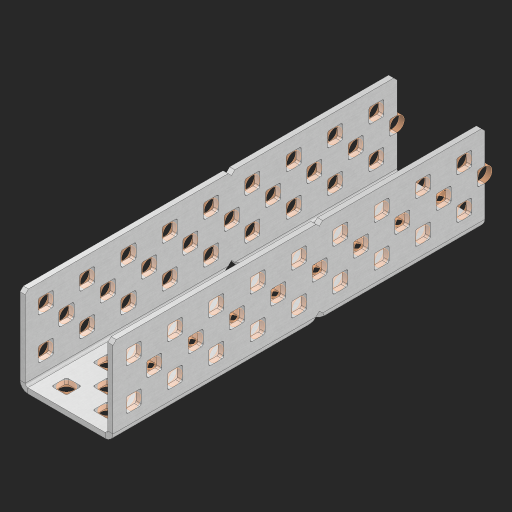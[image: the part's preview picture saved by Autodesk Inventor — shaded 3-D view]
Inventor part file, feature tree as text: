
AUTODESK INVENTOR PART (.ipt)
format: ipt  version: 2023 (Build 270158000, 158)  size: 1,304,064 bytes
history: native  units: in
note: dims shown in document units (in); Inventor stores cm internally (conversion verified against a paired STEP export)
features: other x114, extrude x106, sheet_metal_op x8, sketch x7, mirror x3, pattern_linear x2, chamfer x1
ambient origin geometry x8: Origin, YZ Plane, XZ Plane, XY Plane, X Axis, Y Axis, Z Axis, Center Point
bodies: Solid1 (feature_tree), Body (feature_tree)
feature tree (241):
  sheet_metal_op  "Flanges"
  sheet_metal_op  "Body Pattern"
  pattern_linear  "Center Pattern"  Spacing1=1.0in  [1 undecoded]
  other  "Arc Length"
  mirror  "Notch Mirror"
  pattern_linear  "Notch Pattern"  Spacing1=0.25in  [1 undecoded]
  other  "Diagonal Plane"
  mirror  "Flange 1"
  mirror  "Flange 2"
  chamfer  "End Chamfer"
  sketch  "Sketch1"  dims[d0=1.0in]
  other  "Plate1"
  sketch  "Sketch2"  dims[d1=4.5in]
  other  "Plate2"
  sheet_metal_op  "Bend1"
  sheet_metal_op  "Corner1"
  sketch  "Sketch8"  dims[d2=0.0625in]
  sketch  "Sketch9"  dims[d3=0.0625in]
  other  "Srf91"
  sheet_metal_op  "Body Pattern Sketch"
  other  "Srf92"
  sketch  "Sketch13"  dims[d4=0.0312in]
  sketch  "Sketch15"  dims[d5=0.125in]
  sketch  "Sketch16"  dims[d6=0.0625in d7=1.0in d8=90.0deg d9=0.0312in d10=0.25in d11=0.0625in d12=0.0625in d49=0.182in d50=0.02in d52=0.25in d53=0.0625in d54=0.0in d55=0.172in d56=1.0in d57=0.0in d60=3.5433in d62=0.5in d63=0.7874in d65=0.5in d85=0.1473in d86=0.1782in d88=0.04in d89=0.0625in d90=0.0in d91=0.04in d92=0.0491in d95=2.5in d96=0.04in d97=0.25in d98=45.0deg d99=0.25in d102=2.497in d106=0.182in d107=0.02in d108=0.5in d110=0.0625in d111=0.0in d112=0.172in d113=0.5in d114=0.0in d117=0.5in d118=0.5in d131=0.25in d132=0.25in]
  other  "Srf786"
  other  "Srf889"
  other  "Srf890"
  other  "Srf891"
  other  "Srf892"
  other  "Srf893"
  other  "Srf894"
  other  "Srf895"
  other  "Srf896"
  other  "Srf1315"
  other  "Srf1316"
  other  "Srf1317"
  other  "Srf1325"
  other  "Srf1326"
  other  "Srf1327"
  other  "Srf1328"
  other  "Srf1329"
  other  "Srf1330"
  other  "Srf1331"
  other  "Srf1332"
  other  "Srf1374"
  other  "Srf1375"
  other  "Srf1376"
  other  "Srf1384"
  other  "Srf1385"
  other  "Srf1386"
  other  "Srf1387"
  other  "Srf1388"
  other  "Srf1389"
  other  "Srf1390"
  other  "Srf1391"
  other  "Srf1433"
  other  "Srf1434"
  other  "Srf1473"
  other  "Srf1474"
  other  "Srf1475"
  other  "Srf1476"
  other  "Srf1477"
  other  "Srf1478"
  other  "Srf1479"
  other  "Srf1480"
  other  "Srf1481"
  other  "Srf1500"
  other  "Srf1501"
  other  "Srf1502"
  other  "Srf1503"
  other  "Srf1504"
  other  "Srf1505"
  other  "Srf1506"
  other  "Srf1507"
  other  "Srf1508"
  other  "Srf1509"
  other  "Srf1510"
  other  "Srf1511"
  other  "Srf1512"
  other  "Srf1513"
  other  "Srf1514"
  other  "Srf1515"
  other  "Srf1538"
  other  "Srf1539"
  other  "Srf1540"
  other  "Srf1541"
  other  "Srf1542"
  other  "Srf1543"
  other  "Srf1544"
  other  "Srf1545"
  other  "Srf1546"
  other  "Srf1547"
  other  "Srf1548"
  other  "Srf1549"
  other  "Srf1550"
  other  "Srf1551"
  other  "Srf1552"
  other  "Srf1553"
  other  "Srf1576"
  other  "Srf1577"
  other  "Srf1578"
  other  "Srf1579"
  other  "Srf1580"
  other  "Srf1581"
  other  "Srf1582"
  other  "Srf1583"
  other  "Srf1584"
  other  "Srf1585"
  other  "Srf1586"
  other  "Srf1587"
  other  "Srf1588"
  other  "Srf1589"
  other  "Srf1590"
  other  "Srf1591"
  other  "Srf1614"
  other  "Srf1615"
  other  "Srf1616"
  other  "Srf1617"
  other  "Srf1618"
  other  "Srf1619"
  other  "Srf1620"
  other  "Srf1621"
  other  "Srf1622"
  other  "Srf1623"
  other  "Srf1624"
  other  "Srf1625"
  other  "Srf1626"
  other  "Srf1627"
  other  "Srf1628"
  other  "Srf1629"
  sheet_metal_op  "Body Stamp"
  sheet_metal_op  "Body Circle"
  other  "Center Stamp"
  other  "Center Circle"
  sheet_metal_op  "Notch"
  extrude  "ExtrusionSrf92"  Depth=0.0625in
  extrude  "ExtrusionSrf889"  Depth=0.0625in
  extrude  "ExtrusionSrf890"  Depth=0.182in
  extrude  "ExtrusionSrf891"  Depth=0.02in
  extrude  "ExtrusionSrf892"  Depth=0.25in
  extrude  "ExtrusionSrf893"  Depth=0.0625in
  extrude  "ExtrusionSrf894"  TaperAngle=0.0deg  [1 undecoded]
  extrude  "ExtrusionSrf895"  Depth=0.25in
  extrude  "ExtrusionSrf896"  Depth=1.0in TaperAngle=0.0deg
  extrude  "ExtrusionSrf1315"  Depth=0.25in
  extrude  "ExtrusionSrf1316"  Depth=0.5in
  extrude  "ExtrusionSrf1355"  Depth=0.25in
  extrude  "ExtrusionSrf1356"  Depth=0.25in
  extrude  "ExtrusionSrf1357"  Depth=0.25in
  extrude  "ExtrusionSrf1358"  Depth=0.0625in
  extrude  "ExtrusionSrf1359"  TaperAngle=0.0deg  [1 undecoded]
  extrude  "ExtrusionSrf1360"  Depth=0.25in
  extrude  "ExtrusionSrf1361"  Depth=0.25in
  extrude  "ExtrusionSrf1362"  Depth=2.5in
  extrude  "ExtrusionSrf1363"  Depth=0.25in TaperAngle=45.0deg
  extrude  "ExtrusionSrf1374"  Depth=0.25in
  extrude  "ExtrusionSrf1375"  Depth=0.25in
  extrude  "ExtrusionSrf1414"  Depth=0.182in
  extrude  "ExtrusionSrf1415"  Depth=0.02in
  extrude  "ExtrusionSrf1416"  Depth=0.5in
  extrude  "ExtrusionSrf1417"  Depth=0.0625in
  extrude  "ExtrusionSrf1418"  TaperAngle=0.0deg  [1 undecoded]
  extrude  "ExtrusionSrf1419"  Depth=0.25in
  extrude  "ExtrusionSrf1420"  Depth=0.5in TaperAngle=0.0deg
  extrude  "ExtrusionSrf1421"  Depth=0.5in
  extrude  "ExtrusionSrf1422"  Depth=0.5in
  extrude  "ExtrusionSrf1433"  Depth=0.25in
  extrude  "ExtrusionSrf1434"  Depth=0.25in
  extrude  "ExtrusionSrf1473"  [1 undecoded]
  extrude  "ExtrusionSrf1474"  [1 undecoded]
  extrude  "ExtrusionSrf1475"  [1 undecoded]
  extrude  "ExtrusionSrf1476"  [1 undecoded]
  extrude  "ExtrusionSrf1477"  [1 undecoded]
  extrude  "ExtrusionSrf1478"  [1 undecoded]
  extrude  "ExtrusionSrf1479"  [1 undecoded]
  extrude  "ExtrusionSrf1480"  [1 undecoded]
  extrude  "ExtrusionSrf1481"  [1 undecoded]
  extrude  "ExtrusionSrf1500"  [1 undecoded]
  extrude  "ExtrusionSrf1501"  [1 undecoded]
  extrude  "ExtrusionSrf1502"  [1 undecoded]
  extrude  "ExtrusionSrf1503"  [1 undecoded]
  extrude  "ExtrusionSrf1504"  [1 undecoded]
  extrude  "ExtrusionSrf1505"  [1 undecoded]
  extrude  "ExtrusionSrf1506"  [1 undecoded]
  extrude  "ExtrusionSrf1507"  [1 undecoded]
  extrude  "ExtrusionSrf1508"  [1 undecoded]
  extrude  "ExtrusionSrf1509"  [1 undecoded]
  extrude  "ExtrusionSrf1510"  [1 undecoded]
  extrude  "ExtrusionSrf1511"  [1 undecoded]
  extrude  "ExtrusionSrf1512"  [1 undecoded]
  extrude  "ExtrusionSrf1513"  [1 undecoded]
  extrude  "ExtrusionSrf1514"  [1 undecoded]
  extrude  "ExtrusionSrf1515"  [1 undecoded]
  extrude  "ExtrusionSrf1538"  [1 undecoded]
  extrude  "ExtrusionSrf1539"  [1 undecoded]
  extrude  "ExtrusionSrf1540"  [1 undecoded]
  extrude  "ExtrusionSrf1541"  [1 undecoded]
  extrude  "ExtrusionSrf1542"  [1 undecoded]
  extrude  "ExtrusionSrf1543"  [1 undecoded]
  extrude  "ExtrusionSrf1544"  [1 undecoded]
  extrude  "ExtrusionSrf1545"  [1 undecoded]
  extrude  "ExtrusionSrf1546"  [1 undecoded]
  extrude  "ExtrusionSrf1547"  [1 undecoded]
  extrude  "ExtrusionSrf1548"  [1 undecoded]
  extrude  "ExtrusionSrf1549"  [1 undecoded]
  extrude  "ExtrusionSrf1550"  [1 undecoded]
  extrude  "ExtrusionSrf1551"  [1 undecoded]
  extrude  "ExtrusionSrf1552"  [1 undecoded]
  extrude  "ExtrusionSrf1553"  [1 undecoded]
  extrude  "ExtrusionSrf1576"  [1 undecoded]
  extrude  "ExtrusionSrf1577"  [1 undecoded]
  extrude  "ExtrusionSrf1578"  [1 undecoded]
  extrude  "ExtrusionSrf1579"  [1 undecoded]
  extrude  "ExtrusionSrf1580"  [1 undecoded]
  extrude  "ExtrusionSrf1581"  [1 undecoded]
  extrude  "ExtrusionSrf1582"  [1 undecoded]
  extrude  "ExtrusionSrf1583"  [1 undecoded]
  extrude  "ExtrusionSrf1584"  [1 undecoded]
  extrude  "ExtrusionSrf1585"  [1 undecoded]
  extrude  "ExtrusionSrf1586"  [1 undecoded]
  extrude  "ExtrusionSrf1587"  [1 undecoded]
  extrude  "ExtrusionSrf1588"  [1 undecoded]
  extrude  "ExtrusionSrf1589"  [1 undecoded]
  extrude  "ExtrusionSrf1590"  [1 undecoded]
  extrude  "ExtrusionSrf1591"  [1 undecoded]
  extrude  "ExtrusionSrf1614"  [1 undecoded]
  extrude  "ExtrusionSrf1615"  [1 undecoded]
  extrude  "ExtrusionSrf1616"  [1 undecoded]
  extrude  "ExtrusionSrf1617"  [1 undecoded]
  extrude  "ExtrusionSrf1618"  [1 undecoded]
  extrude  "ExtrusionSrf1619"  [1 undecoded]
  extrude  "ExtrusionSrf1620"  [1 undecoded]
  extrude  "ExtrusionSrf1621"  [1 undecoded]
  extrude  "ExtrusionSrf1622"  [1 undecoded]
  extrude  "ExtrusionSrf1623"  [1 undecoded]
  extrude  "ExtrusionSrf1624"  [1 undecoded]
  extrude  "ExtrusionSrf1625"  [1 undecoded]
  extrude  "ExtrusionSrf1626"  [1 undecoded]
  extrude  "ExtrusionSrf1627"  [1 undecoded]
  extrude  "ExtrusionSrf1628"  [1 undecoded]
  extrude  "ExtrusionSrf1629"  [1 undecoded]
note: 78 required parameter values undecoded (feature->parameter linkage not recoverable at this tier; creation-order binding heuristic only, values carry confidence <= 0.55)
